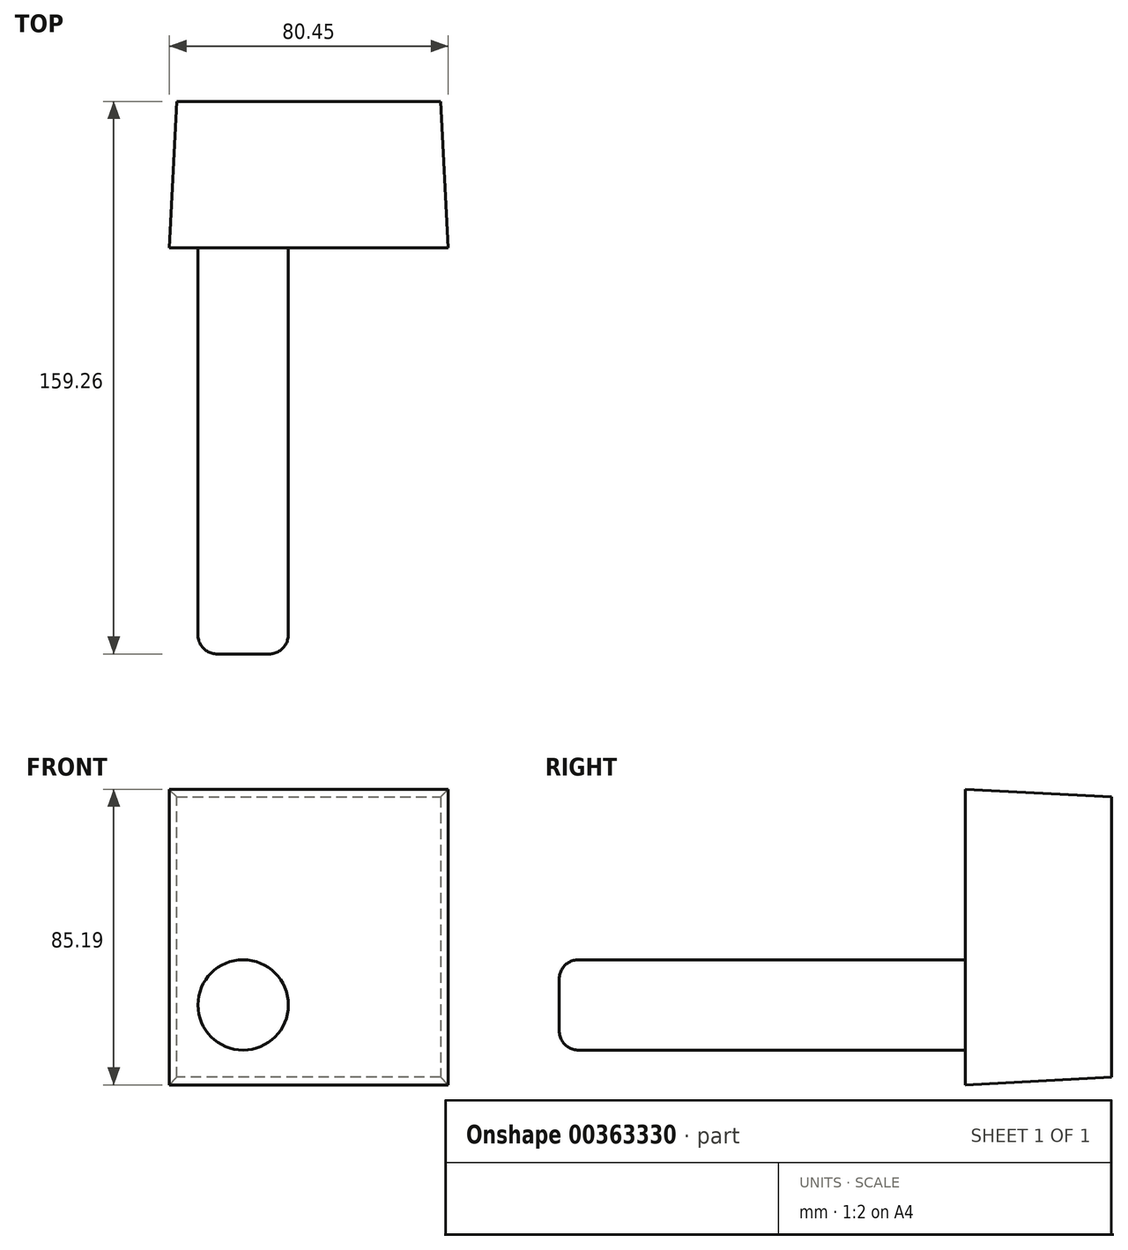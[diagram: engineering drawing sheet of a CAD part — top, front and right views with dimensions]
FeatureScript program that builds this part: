
annotation { "Feature Type Name" : "Feature", "Feature Type Description" : "" }
export const myFeature = defineFeature(function(context is Context, id is Id, definition is map)
    precondition{}
    {
        {
            var Q0;
            Q0=qCreatedBy(makeId("Front.planeOp"),FACE);
            var sketch = newSketch(context, id + "F0", { "sketchPlane" : qUnion([Q0])});
            skLineSegment(sketch, "E0.bottom", {"start": v(-44.3, 43.07) * mm, "end": v(31.74, 43.07) * mm});
            skLineSegment(sketch, "E0.top", {"start": v(-44.3, -37.7) * mm, "end": v(31.74, -37.7) * mm});
            skLineSegment(sketch, "E0.left", {"start": v(-44.3, 43.07) * mm, "end": v(-44.3, -37.7) * mm});
            skLineSegment(sketch, "E0.right", {"start": v(31.74, 43.07) * mm, "end": v(31.74, -37.7) * mm});
            skSolve(sketch);
        }
        {
            var Q0;
            Q0 = qSketchRegion(id + "F0", true);
            extrude(context, id + "F1", {"entities" : qUnion([Q0]), "depth" : 42.16 * mm, "hasDraft" : true, "draftAngle" : 3 * degree});
        }
        {
            var Q0;
            Q0=makeQuery(id+"F1.opExtrude","CAP_FACE",FACE,{"disambiguationData":[OSD([sQuery(id+"F0.wireOp",EDGE,"E0.bottom"),sQuery(id+"F0.wireOp",EDGE,"E0.top"),sQuery(id+"F0.wireOp",EDGE,"E0.left"),sQuery(id+"F0.wireOp",EDGE,"E0.right")])],"isStart":false});
            var sketch = newSketch(context, id + "F2", { "sketchPlane" : qUnion([Q0])});
            skCircle(sketch, "E1", {"center": v(-25.18, -16.87) * mm, "radius": 13.03 * mm});
            skSolve(sketch);
        }
        {
            var Q0;
            Q0 = qSketchRegion(id + "F2", true);
            extrude(context, id + "F3", {"entities" : qUnion([Q0]), "operationType" : NewBodyOperationType.ADD, "depth" : 117.1 * mm});
        }
        {
            var Q0;
            Q0=makeQuery(id+"F3.opExtrude","CAP_EDGE",EDGE,{"disambiguationData":[OSD([sQuery(id+"F2.wireOp",EDGE,"E1")])],"isStart":false});
            fillet(context, id + "F4", {"entities" : qUnion([Q0]), "radius" : 5.52 * mm, "tangentPropagation" : true, "allowEdgeOverflow" : false});
        }
    });
